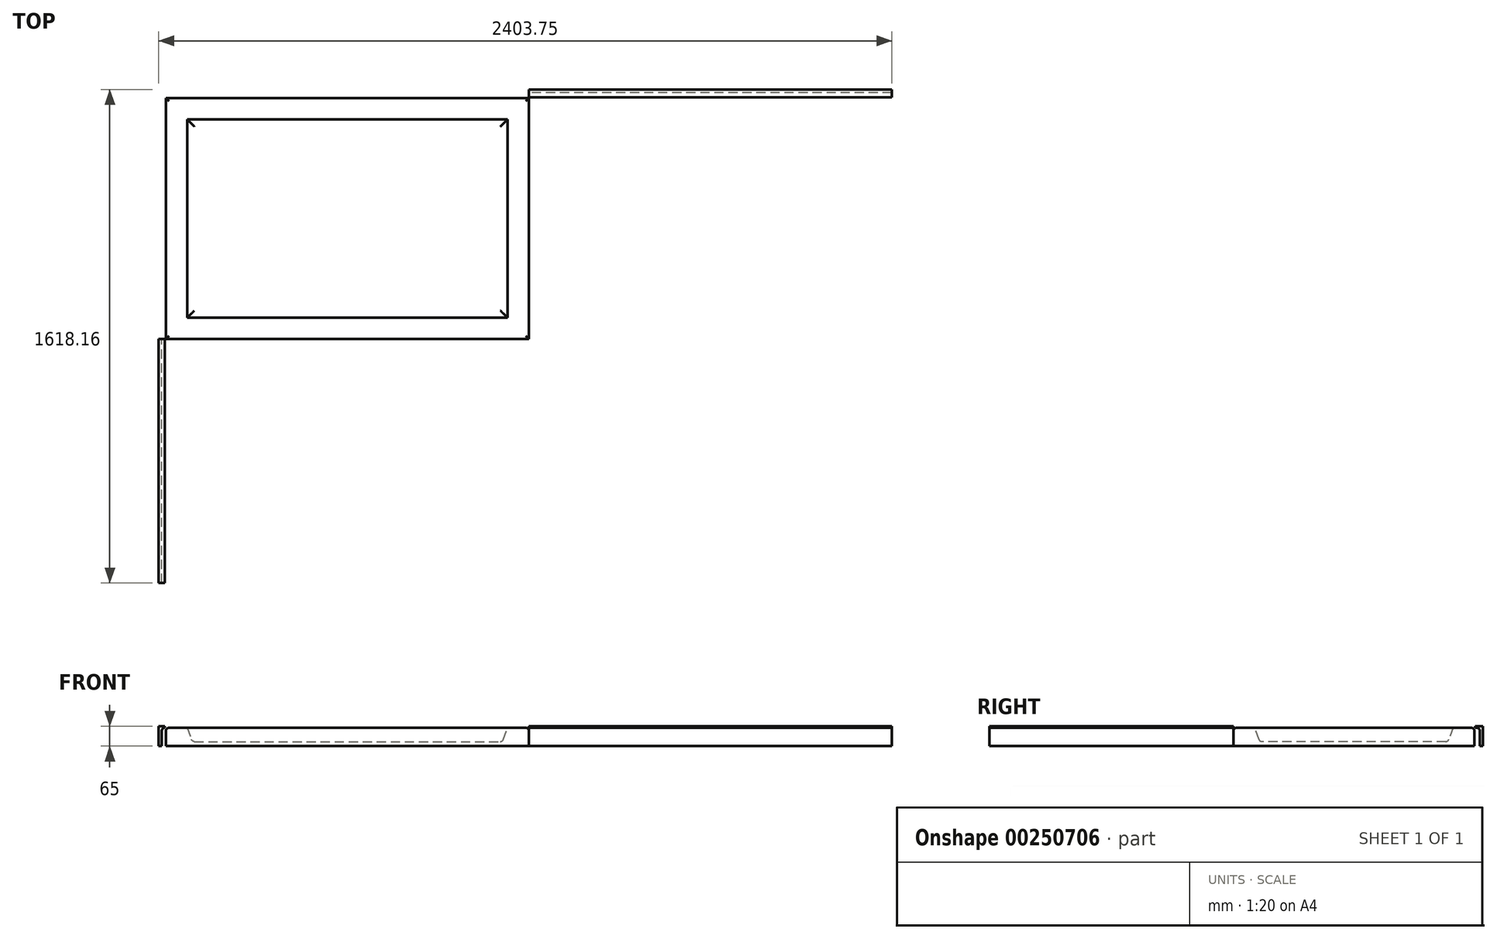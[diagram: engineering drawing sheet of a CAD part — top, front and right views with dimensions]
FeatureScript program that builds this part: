
annotation { "Feature Type Name" : "Feature", "Feature Type Description" : "" }
export const myFeature = defineFeature(function(context is Context, id is Id, definition is map)
    precondition{}
    {
        {
            var Q0;
            Q0=qCreatedBy(makeId("Top.planeOp"),FACE);
            var sketch = newSketch(context, id + "F0", { "sketchPlane" : qUnion([Q0])});
            skLineSegment(sketch, "E0.bottom", {"start": v(0, 0) * mm, "end": v(1190, 0) * mm});
            skLineSegment(sketch, "E0.top", {"start": v(0, 790) * mm, "end": v(1190, 790) * mm});
            skLineSegment(sketch, "E0.left", {"start": v(0, 0) * mm, "end": v(0, 790) * mm});
            skLineSegment(sketch, "E0.right", {"start": v(1190, 0) * mm, "end": v(1190, 790) * mm});
            skSolve(sketch);
        }
        {
            var Q0;
            Q0=makeQuery(id+"F0.imprint","IMPRINT",FACE,{"disambiguationData":[TD([[makeQuery(id+"F0.imprint","IMPRINT",EDGE,{"derivedFrom":sQuery(id+"F0.wireOp",EDGE,"E0.bottom")}),1.0]])]});
            extrude(context, id + "F1", {"entities" : qUnion([Q0]), "depth" : 60 * mm});
        }
        {
            var Q0;
            Q0=makeQuery(id+"F1.opExtrude","CAP_FACE",FACE,{"disambiguationData":[OSD([sQuery(id+"F0.wireOp",EDGE,"E0.bottom"),sQuery(id+"F0.wireOp",EDGE,"E0.top"),sQuery(id+"F0.wireOp",EDGE,"E0.left"),sQuery(id+"F0.wireOp",EDGE,"E0.right")])],"isStart":false});
            var sketch = newSketch(context, id + "F2", { "sketchPlane" : qUnion([Q0])});
            skLineSegment(sketch, "E1.bottom", {"start": v(70, 720) * mm, "end": v(1120, 720) * mm});
            skLineSegment(sketch, "E1.top", {"start": v(70, 70) * mm, "end": v(1120, 70) * mm});
            skLineSegment(sketch, "E1.left", {"start": v(70, 720) * mm, "end": v(70, 70) * mm});
            skLineSegment(sketch, "E1.right", {"start": v(1120, 720) * mm, "end": v(1120, 70) * mm});
            skSolve(sketch);
        }
        {
            var Q0;
            Q0=makeQuery(id+"F2.imprint","IMPRINT",FACE,{"disambiguationData":[TD([[makeQuery(id+"F2.imprint","IMPRINT",EDGE,{"derivedFrom":sQuery(id+"F2.wireOp",EDGE,"E1.bottom")}),-1.0]])]});
            extrude(context, id + "F3", {"entities" : qUnion([Q0]), "operationType" : NewBodyOperationType.REMOVE, "oppositeDirection" : true, "depth" : 45 * mm, "hasDraft" : true, "draftAngle" : 20 * degree, "draftPullDirection" : true});
        }
        {
            var Q0;
            Q0=makeQuery(id+"F1.opExtrude","CAP_EDGE",EDGE,{"disambiguationData":[OSD([sQuery(id+"F0.wireOp",EDGE,"E0.left")])],"isStart":false});
            var Q1;
            Q1=makeQuery(id+"F1.opExtrude","CAP_EDGE",EDGE,{"disambiguationData":[OSD([sQuery(id+"F0.wireOp",EDGE,"E0.top")])],"isStart":false});
            var Q2;
            Q2=makeQuery(id+"F1.opExtrude","CAP_EDGE",EDGE,{"disambiguationData":[OSD([sQuery(id+"F0.wireOp",EDGE,"E0.right")])],"isStart":false});
            var Q3;
            Q3=makeQuery(id+"F1.opExtrude","CAP_EDGE",EDGE,{"disambiguationData":[OSD([sQuery(id+"F0.wireOp",EDGE,"E0.bottom")])],"isStart":false});
            var Q4;
            Q4=makeQuery(id+"F3.boolean.opBoolean","COPY",EDGE,{"derivedFrom":makeQuery(id+"F3.opExtrude","CAP_EDGE",EDGE,{"disambiguationData":[OSD([sQuery(id+"F2.wireOp",EDGE,"E1.left")])],"isStart":true})});
            var Q5;
            Q5=makeQuery(id+"F3.boolean.opBoolean","COPY",EDGE,{"derivedFrom":makeQuery(id+"F3.opExtrude","CAP_EDGE",EDGE,{"disambiguationData":[OSD([sQuery(id+"F2.wireOp",EDGE,"E1.bottom")])],"isStart":true})});
            var Q6;
            Q6=makeQuery(id+"F3.boolean.opBoolean","COPY",EDGE,{"derivedFrom":makeQuery(id+"F3.opExtrude","CAP_EDGE",EDGE,{"disambiguationData":[OSD([sQuery(id+"F2.wireOp",EDGE,"E1.right")])],"isStart":true})});
            var Q7;
            Q7=makeQuery(id+"F3.boolean.opBoolean","COPY",EDGE,{"derivedFrom":makeQuery(id+"F3.opExtrude","CAP_EDGE",EDGE,{"disambiguationData":[OSD([sQuery(id+"F2.wireOp",EDGE,"E1.top")])],"isStart":true})});
            fillet(context, id + "F4", {"entities" : qUnion([Q0, Q1, Q2, Q3, Q4, Q5, Q6, Q7]), "radius" : 10 * mm, "tangentPropagation" : true, "allowEdgeOverflow" : false});
        }
        {
            var Q0;
            Q0=makeQuery(id+"F3.boolean.opBoolean","COPY",EDGE,{"derivedFrom":makeQuery(id+"F3.opExtrude","CAP_EDGE",EDGE,{"disambiguationData":[OSD([sQuery(id+"F2.wireOp",EDGE,"E1.left")])],"isStart":false})});
            var Q1;
            Q1=makeQuery(id+"F3.boolean.opBoolean","COPY",EDGE,{"derivedFrom":makeQuery(id+"F3.opExtrude","CAP_EDGE",EDGE,{"disambiguationData":[OSD([sQuery(id+"F2.wireOp",EDGE,"E1.bottom")])],"isStart":false})});
            var Q2;
            Q2=makeQuery(id+"F3.boolean.opBoolean","COPY",EDGE,{"derivedFrom":makeQuery(id+"F3.opExtrude","CAP_EDGE",EDGE,{"disambiguationData":[OSD([sQuery(id+"F2.wireOp",EDGE,"E1.right")])],"isStart":false})});
            var Q3;
            Q3=makeQuery(id+"F3.boolean.opBoolean","COPY",EDGE,{"derivedFrom":makeQuery(id+"F3.opExtrude","CAP_EDGE",EDGE,{"disambiguationData":[OSD([sQuery(id+"F2.wireOp",EDGE,"E1.top")])],"isStart":false})});
            fillet(context, id + "F5", {"entities" : qUnion([Q0, Q1, Q2, Q3]), "radius" : 10 * mm, "tangentPropagation" : true, "allowEdgeOverflow" : false});
        }
        {
            var Q0;
            Q0=qCreatedBy(makeId("Front.planeOp"),FACE);
            var sketch = newSketch(context, id + "F6", { "sketchPlane" : qUnion([Q0])});
            skLineSegment(sketch, "E2.bottom", {"start": v(-23.75, 0) * mm, "end": v(-13.75, 0) * mm});
            skLineSegment(sketch, "E2.top", {"start": v(-23.75, 65) * mm, "end": v(-13.75, 65) * mm});
            skLineSegment(sketch, "E2.left", {"start": v(-23.75, 0) * mm, "end": v(-23.75, 65) * mm});
            skLineSegment(sketch, "E2.right", {"start": v(-13.75, 0) * mm, "end": v(-13.75, 50) * mm});
            skLineSegment(sketch, "E3.bottom", {"start": v(-13.75, 65) * mm, "end": v(-3.75, 65) * mm});
            skLineSegment(sketch, "E3.top", {"start": v(-3.75, 60) * mm, "end": v(-3.75, 60) * mm});
            skLineSegment(sketch, "E3.right", {"start": v(-3.75, 65) * mm, "end": v(-3.75, 60) * mm});
            skArc(sketch, "E4.filletArc", {"start": v(-3.75, 60) * mm, "mid": v(-10.82, 57.07) * mm, "end": v(-13.75, 50) * mm});
            skSolve(sketch);
        }
        {
            var Q0;
            Q0=makeQuery(id+"F6.imprint","IMPRINT",FACE,{"disambiguationData":[TD([[makeQuery(id+"F6.imprint","IMPRINT",EDGE,{"derivedFrom":sQuery(id+"F6.wireOp",EDGE,"E2.bottom")}),1.0]])]});
            extrude(context, id + "F7", {"entities" : qUnion([Q0]), "depth" : 800 * mm});
        }
        {
            var Q0;
            Q0=makeQuery(id+"F1.opExtrude","SWEPT_FACE",FACE,{"disambiguationData":[OSD([sQuery(id+"F0.wireOp",EDGE,"E0.right")])]});
            var sketch = newSketch(context, id + "F8", { "sketchPlane" : qUnion([Q0])});
            skLineSegment(sketch, "E5.top", {"start": v(808.16, 0) * mm, "end": v(818.16, 0) * mm});
            skLineSegment(sketch, "E5.left", {"start": v(808.16, 50) * mm, "end": v(808.16, 0) * mm});
            skLineSegment(sketch, "E5.right", {"start": v(818.16, 50) * mm, "end": v(818.16, 0) * mm});
            skLineSegment(sketch, "E6.bottom", {"start": v(793.16, 65) * mm, "end": v(818.16, 65) * mm});
            skLineSegment(sketch, "E6.top", {"start": v(793.16, 60) * mm, "end": v(798.16, 60) * mm});
            skLineSegment(sketch, "E6.left", {"start": v(793.16, 65) * mm, "end": v(793.16, 60) * mm});
            skArc(sketch, "E7.filletArc", {"start": v(808.16, 50) * mm, "mid": v(805.23, 57.07) * mm, "end": v(798.16, 60) * mm});
            skLineSegment(sketch, "E8", {"start": v(818.16, 65) * mm, "end": v(818.16, 50) * mm});
            skSolve(sketch);
        }
        {
            var Q0;
            Q0=makeQuery(id+"F8.imprint","IMPRINT",FACE,{"disambiguationData":[TD([[makeQuery(id+"F8.imprint","IMPRINT",EDGE,{"derivedFrom":sQuery(id+"F8.wireOp",EDGE,"E5.top")}),1.0]])]});
            extrude(context, id + "F9", {"entities" : qUnion([Q0]), "depth" : 1190 * mm});
        }
    });
